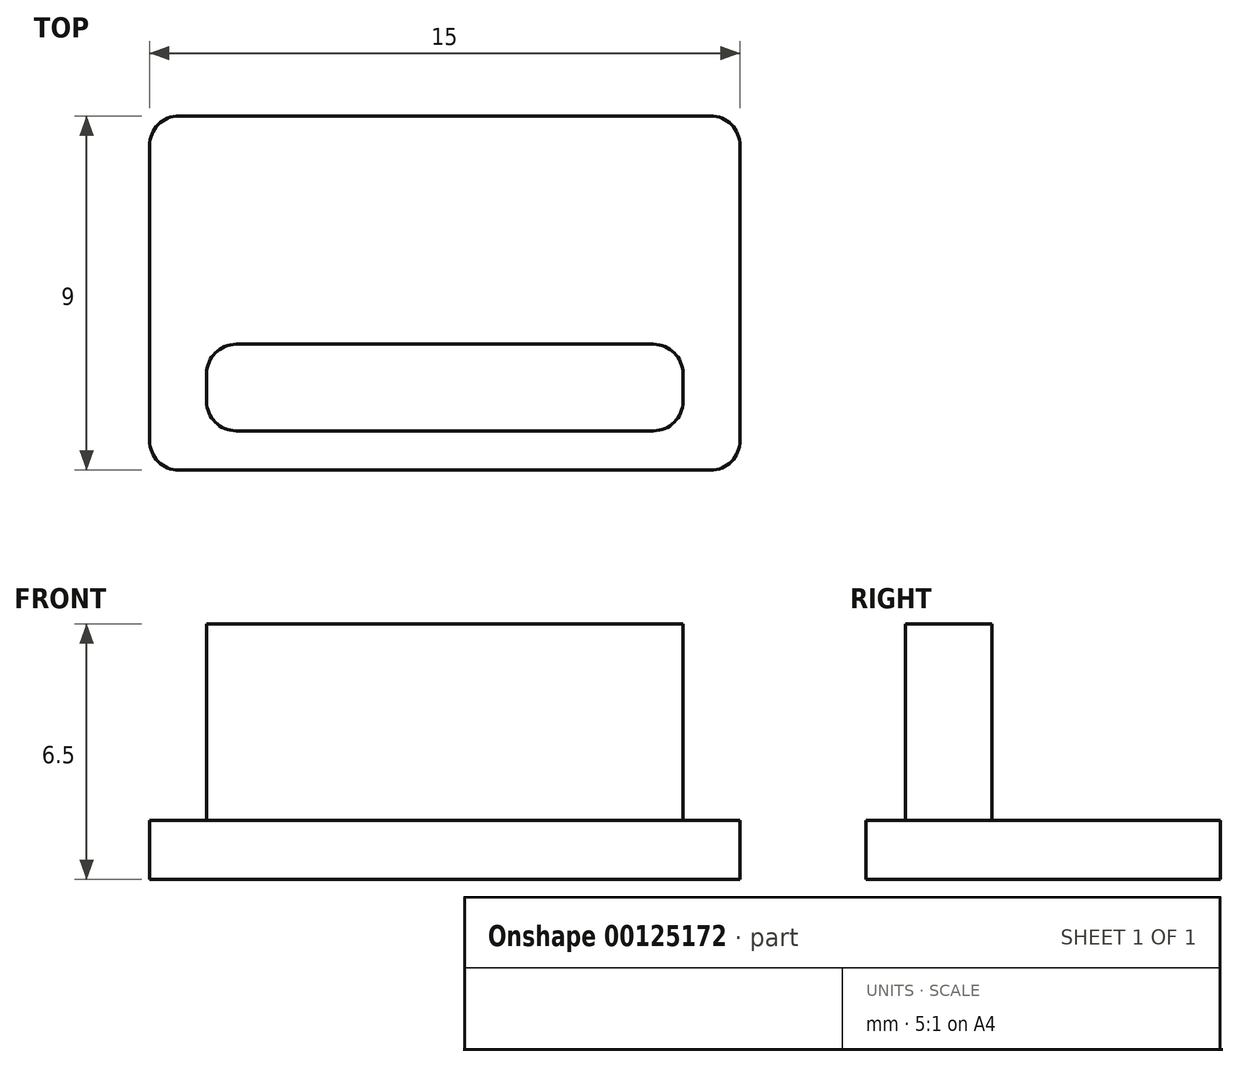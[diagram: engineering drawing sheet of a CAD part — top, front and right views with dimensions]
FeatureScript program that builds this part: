
annotation { "Feature Type Name" : "Feature", "Feature Type Description" : "" }
export const myFeature = defineFeature(function(context is Context, id is Id, definition is map)
    precondition{}
    {
        {
            var Q0;
            Q0=qCreatedBy(makeId("Top.planeOp"),FACE);
            var sketch = newSketch(context, id + "F0", { "sketchPlane" : qUnion([Q0])});
            skLineSegment(sketch, "E0.bottom", {"start": v(6.05, -1.1) * mm, "end": v(-6.05, -1.1) * mm});
            skLineSegment(sketch, "E0.top", {"start": v(6.05, 1.1) * mm, "end": v(-6.05, 1.1) * mm});
            skLineSegment(sketch, "E0.left", {"start": v(6.05, -1.1) * mm, "end": v(6.05, 1.1) * mm});
            skLineSegment(sketch, "E0.right", {"start": v(-6.05, -1.1) * mm, "end": v(-6.05, 1.1) * mm});
            skPoint(sketch, "E0.middle", {"position": v(0, 0) * mm});
            skLineSegment(sketch, "E1.bottom", {"start": v(7.5, -2.1) * mm, "end": v(-7.5, -2.1) * mm});
            skLineSegment(sketch, "E1.top", {"start": v(7.5, 6.9) * mm, "end": v(-7.5, 6.9) * mm});
            skLineSegment(sketch, "E1.left", {"start": v(7.5, -2.1) * mm, "end": v(7.5, 6.9) * mm});
            skLineSegment(sketch, "E1.right", {"start": v(-7.5, -2.1) * mm, "end": v(-7.5, 6.9) * mm});
            skPoint(sketch, "E1.middle", {"position": v(0, 2.4) * mm});
            skSolve(sketch);
        }
        {
            var Q0;
            Q0=makeQuery(id+"F0.imprint","IMPRINT",FACE,{"disambiguationData":[TD([[makeQuery(id+"F0.imprint","IMPRINT",EDGE,{"derivedFrom":sQuery(id+"F0.wireOp",EDGE,"E0.bottom")}),-1.0]])]});
            extrude(context, id + "F1", {"entities" : qUnion([Q0]), "depth" : 5 * mm});
        }
        {
            var Q0;
            Q0=makeQuery(id+"F0.imprint","IMPRINT",FACE,{"disambiguationData":[TD([[makeQuery(id+"F0.imprint","IMPRINT",EDGE,{"derivedFrom":sQuery(id+"F0.wireOp",EDGE,"E0.bottom")}),1.0]])]});
            var Q1;
            Q1=makeQuery(id+"F0.imprint","IMPRINT",FACE,{"disambiguationData":[TD([[makeQuery(id+"F0.imprint","IMPRINT",EDGE,{"derivedFrom":sQuery(id+"F0.wireOp",EDGE,"E0.bottom")}),-1.0]])]});
            extrude(context, id + "F2", {"entities" : qUnion([Q0, Q1]), "operationType" : NewBodyOperationType.ADD, "oppositeDirection" : true, "depth" : 1.5 * mm});
        }
        {
            var Q0;
            Q0=makeQuery(id+"F1.opExtrude","SWEPT_EDGE",EDGE,{"disambiguationData":[OSD([sQuery(id+"F0.wireOp",EDGE,"E0.top"),sQuery(id+"F0.wireOp",EDGE,"E0.right")])]});
            var Q1;
            Q1=makeQuery(id+"F1.opExtrude","SWEPT_EDGE",EDGE,{"disambiguationData":[OSD([sQuery(id+"F0.wireOp",EDGE,"E0.bottom"),sQuery(id+"F0.wireOp",EDGE,"E0.right")])]});
            var Q2;
            Q2=makeQuery(id+"F1.opExtrude","SWEPT_EDGE",EDGE,{"disambiguationData":[OSD([sQuery(id+"F0.wireOp",EDGE,"E0.top"),sQuery(id+"F0.wireOp",EDGE,"E0.left")])]});
            var Q3;
            Q3=makeQuery(id+"F1.opExtrude","SWEPT_EDGE",EDGE,{"disambiguationData":[OSD([sQuery(id+"F0.wireOp",EDGE,"E0.bottom"),sQuery(id+"F0.wireOp",EDGE,"E0.left")])]});
            var Q4;
            Q4=makeQuery(id+"F2.opExtrude","SWEPT_EDGE",EDGE,{"disambiguationData":[OSD([sQuery(id+"F0.wireOp",EDGE,"E1.bottom"),sQuery(id+"F0.wireOp",EDGE,"E1.left")])]});
            var Q5;
            Q5=makeQuery(id+"F2.opExtrude","SWEPT_EDGE",EDGE,{"disambiguationData":[OSD([sQuery(id+"F0.wireOp",EDGE,"E1.top"),sQuery(id+"F0.wireOp",EDGE,"E1.left")])]});
            var Q6;
            Q6=makeQuery(id+"F2.opExtrude","SWEPT_EDGE",EDGE,{"disambiguationData":[OSD([sQuery(id+"F0.wireOp",EDGE,"E1.top"),sQuery(id+"F0.wireOp",EDGE,"E1.right")])]});
            var Q7;
            Q7=makeQuery(id+"F2.opExtrude","SWEPT_EDGE",EDGE,{"disambiguationData":[OSD([sQuery(id+"F0.wireOp",EDGE,"E1.bottom"),sQuery(id+"F0.wireOp",EDGE,"E1.right")])]});
            fillet(context, id + "F3", {"entities" : qUnion([Q0, Q1, Q2, Q3, Q4, Q5, Q6, Q7]), "radius" : 0.75 * mm, "tangentPropagation" : true, "allowEdgeOverflow" : false});
        }
    });
